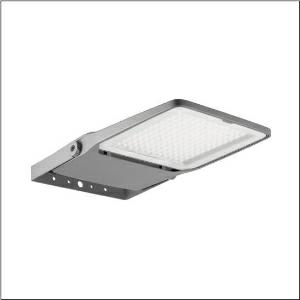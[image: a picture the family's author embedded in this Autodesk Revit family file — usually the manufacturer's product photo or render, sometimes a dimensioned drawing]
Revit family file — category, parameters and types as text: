
# Revit family: floodlight_fl_20_midi___rs05_5xa7682g3h2ac_e142
name_source: partatom
category: Lighting Fixtures
units: mm (PartAtom-declared; Revit-internal decimal feet)

## family parameters
Cut with Voids When Loaded = No
Host = Face
Light Source = No
Part Type = Normal
Room Calculation Point = No
Round Connector Dimension = Use Diameter
Shared = No

## types (1)
- --- (1 x LED 5000K / CRI = 70 (unbekannt), 39000 lm, 5000K)
    Apparent Load = 306 VA
    CIE Flux Codes = 81 94 99 100 100
    Color Rendering = 70
    Color Temperature = 5000K
    Default Elevation = 1800 mm
    Description = Floodlight FL 20 midi, floodlight, primary light control with lens, of plastic, primary optical cover: protective disc, of toughened safety glass, transparent, light distribution: RS05, light emission: direct distribution, primary light characteristic: rotationally symmetric, installation type: surface-mounted, LED High Power LED, rated luminous flux: 39.000 lm, light colour: 750, colour temperature: 5000K, control gear: ECG Plus, control: overheat protection, power reduction, digital communication interface, time-dependent luminous flux control, flexible luminous flux parameterisation, electronic power reduction, with terminal, 10-pole, max. 2.5mm², mains connection: 220..240V, AC, 50/60Hz, rated input power: 306W, LED unit, of diecast aluminium, powder-coated, Siteco® metallic grey (DB 702S), length: 731 mm, width: 450 mm, height: 76mm, housing frame, of diecast aluminium, powder-coated, Siteco® metallic grey (DB 702S), wall fastening, DALIprotection rating (complete): IP66, insulation class (complete): insulation class II (safety insulation), certification: CE, ENEC, VDE, protection symbol: D, permissible ambient temperature for indoor applications: -40..+40°C, permissible ambient temperature for outdoor applications: -40..+50°C, standard: DIN EN 12944, packaging unit: 1 piece

Light Distribution: RS05
    Height = 76 mm
    Lamp = 1 x LED 5000K / CRI >= 70 (unbekannt)
    Lamp Light Flux = 39000 lm
    Lamp count = 1
    Length = 731 mm
    Luminous efficacy = 128 lm/W
    Manufacturer = Siteco
    ModVariant = No
    Model = 5XA7682G3H2AC
    Number of Poles = 1
    OnlyDefault = Yes
    Power Factor = 1
    Product Name = Floodlight FL 20 midi | RS05
    Product group = floodlight | pylon top
    ProductGroupID = 6101
    Protection Class = Protection class II
    Protection Degree = IP 66
    RLX_Detail_Level = 1
    RlxData = <blob elided: 86717 chars, md5=ac9b32d5>
    Socket = socket
    Standby Power = 0 W
    System Light Flux = 39000 lm
    System Power = 306 W
    Type Comments = factory setting: luminous flux: 100 % | dim-lin: 254 | 700 mA
    Type Image = l_1005944.jpg
    URL = http://relux.com
    VarID = @adj_141633
    Voltage = 0 V
    Weight = 0.00 kg
    Width = 450 mm

## geometry (parser evidence)
native form markers: Blend x4, Sweep x13
no freeform markers — native parametric forms only
